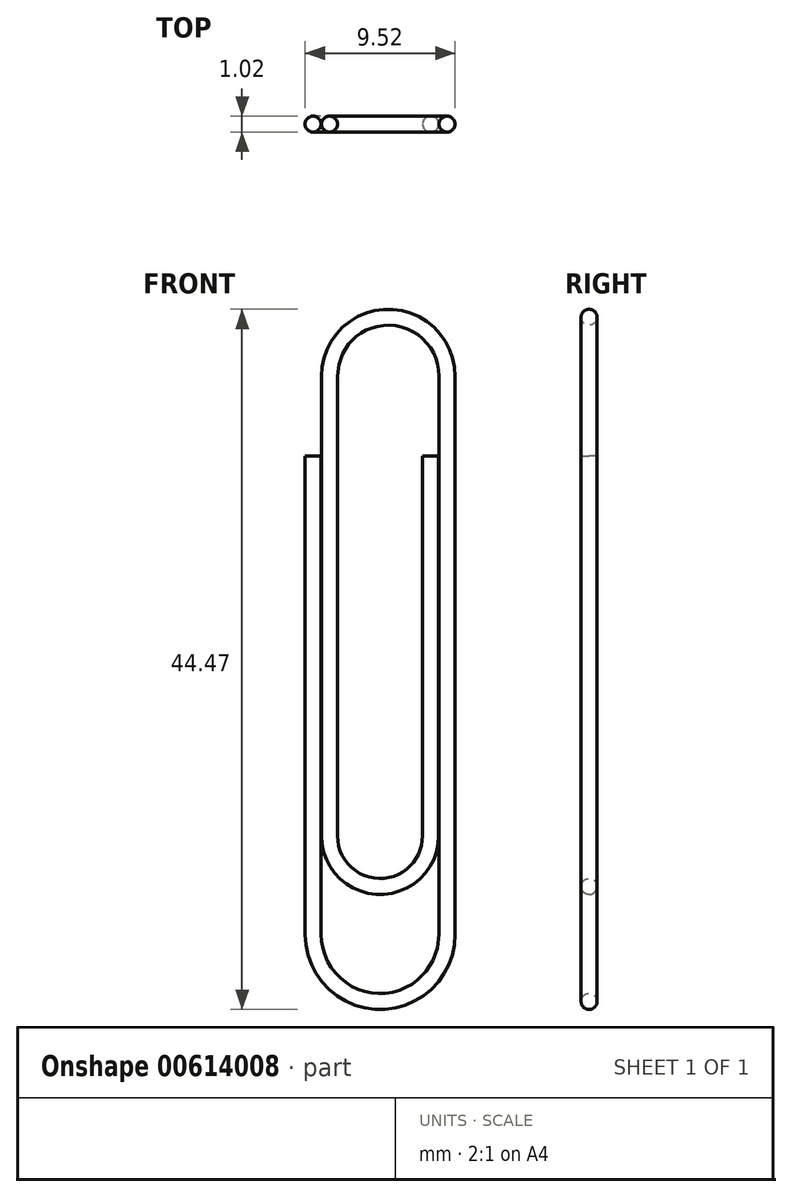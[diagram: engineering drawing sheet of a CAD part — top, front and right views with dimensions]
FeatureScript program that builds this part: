
annotation { "Feature Type Name" : "Feature", "Feature Type Description" : "" }
export const myFeature = defineFeature(function(context is Context, id is Id, definition is map)
    precondition{}
    {
        {
            var Q0;
            Q0=qCreatedBy(makeId("Front.planeOp"),FACE);
            var sketch = newSketch(context, id + "F0", { "sketchPlane" : qUnion([Q0])});
            skPoint(sketch, "E0", {"position": v(0, 0) * mm});
            skPoint(sketch, "E1", {"position": v(4.76, 0) * mm});
            skPoint(sketch, "E2", {"position": v(-4.76, 0) * mm});
            skLineSegment(sketch, "E3", {"start": v(-4.76, 0) * mm, "end": v(4.76, 0) * mm});
            skLineSegment(sketch, "E4", {"start": v(-4.76, 3.9) * mm, "end": v(-4.76, 34.3) * mm});
            skLineSegment(sketch, "E5", {"start": v(4.76, 3.9) * mm, "end": v(4.76, 39.37) * mm});
            skLineSegment(sketch, "E6.0", {"start": v(3.72, 10.16) * mm, "end": v(3.72, 34.3) * mm});
            skLineSegment(sketch, "E7.0", {"start": v(2.7, 10.16) * mm, "end": v(2.7, 34.3) * mm});
            skLineSegment(sketch, "E8.0", {"start": v(-3.72, 10.16) * mm, "end": v(-3.72, 39.37) * mm});
            skLineSegment(sketch, "E9.0", {"start": v(-2.7, 10.16) * mm, "end": v(-2.7, 39.37) * mm});
            skPoint(sketch, "E10", {"position": v(2.7, 34.3) * mm});
            skLineSegment(sketch, "E11", {"start": v(2.7, 34.3) * mm, "end": v(3.72, 34.3) * mm});
            skLineSegment(sketch, "E12", {"start": v(-3.75, 34.3) * mm, "end": v(-4.76, 34.3) * mm});
            skPoint(sketch, "E13", {"position": v(-2.7, 10.16) * mm});
            skPoint(sketch, "E14", {"position": v(2.7, 10.16) * mm});
            skPoint(sketch, "E15", {"position": v(0, 7.45) * mm});
            skArc(sketch, "E16", {"start": v(-2.7, 10.16) * mm, "mid": v(0, 7.45) * mm, "end": v(2.7, 10.16) * mm});
            skPoint(sketch, "E17", {"position": v(0, 6.44) * mm});
            skArc(sketch, "E18", {"start": v(-3.72, 10.16) * mm, "mid": v(0, 6.44) * mm, "end": v(3.72, 10.16) * mm});
            skPoint(sketch, "E19", {"position": v(0, 3.9) * mm});
            skArc(sketch, "E20", {"start": v(-4.76, 3.9) * mm, "mid": v(0, -0.86) * mm, "end": v(4.76, 3.9) * mm});
            skArc(sketch, "E21", {"start": v(-3.75, 3.9) * mm, "mid": v(0, 0.15) * mm, "end": v(3.75, 3.9) * mm});
            skLineSegment(sketch, "E22.trimOffspring", {"start": v(-3.75, 3.9) * mm, "end": v(-3.75, 34.3) * mm});
            skLineSegment(sketch, "E23.trimOffspring", {"start": v(3.75, 3.9) * mm, "end": v(3.75, 39.37) * mm});
            skArc(sketch, "E24", {"start": v(3.75, 39.37) * mm, "mid": v(0.52, 42.6) * mm, "end": v(-2.7, 39.37) * mm});
            skArc(sketch, "E25", {"start": v(4.76, 39.37) * mm, "mid": v(0.52, 43.61) * mm, "end": v(-3.72, 39.37) * mm});
            skSolve(sketch);
        }
        {
            var Q0;
            {var subQ4=sQuery(id+"F0.wireOp",EDGE,"E4");Q0=makeQuery(id+"F0.imprint","IMPRINT",FACE,{"disambiguationData":[TD([[makeQuery(id+"F0.imprint","IMPRINT",EDGE,{"derivedFrom":subQ4}),-1.0]])]});}
            extrude(context, id + "F1", {"entities" : qUnion([Q0]), "depth" : 1.02 * mm, "offsetDistance" : 25.4 * mm});
        }
        {
            var Q0;
            Q0 = qSketchRegion(id + "F0", true);
            extrude(context, id + "F2", {"entities" : qUnion([Q0]), "operationType" : NewBodyOperationType.ADD, "depth" : 1.02 * mm, "offsetDistance" : 25.4 * mm});
        }
        {
            var Q0;
            Q0=makeQuery(id+"F1.opExtrude","CAP_EDGE",EDGE,{"disambiguationData":[OSD([sQuery(id+"F0.wireOp",EDGE,"E5")])],"isStart":false});
            fillet(context, id + "F3", {"entities" : qUnion([Q0]), "radius" : 0.5 * mm, "tangentPropagation" : true, "allowEdgeOverflow" : false});
        }
        {
            var Q0;
            Q0=makeQuery(id+"F1.opExtrude","CAP_EDGE",EDGE,{"disambiguationData":[OSD([sQuery(id+"F0.wireOp",EDGE,"E5")])],"isStart":true});
            fillet(context, id + "F4", {"entities" : qUnion([Q0]), "radius" : 0.5 * mm, "tangentPropagation" : true, "allowEdgeOverflow" : false});
        }
        {
            var Q0;
            Q0=makeQuery(id+"F1.opExtrude","CAP_EDGE",EDGE,{"disambiguationData":[OSD([sQuery(id+"F0.wireOp",EDGE,"E23.trimOffspring")])],"isStart":true});
            fillet(context, id + "F5", {"entities" : qUnion([Q0]), "radius" : 0.5 * mm, "tangentPropagation" : true, "allowEdgeOverflow" : false});
        }
        {
            var Q0;
            Q0=makeQuery(id+"F1.opExtrude","CAP_EDGE",EDGE,{"disambiguationData":[OSD([sQuery(id+"F0.wireOp",EDGE,"E21")])],"isStart":false});
            var Q1;
            Q1=makeQuery(id+"F1.opExtrude","CAP_EDGE",EDGE,{"disambiguationData":[OSD([sQuery(id+"F0.wireOp",EDGE,"E23.trimOffspring")])],"isStart":false});
            fillet(context, id + "F6", {"entities" : qUnion([Q0, Q1]), "radius" : 0.5 * mm, "tangentPropagation" : true, "allowEdgeOverflow" : false});
        }
    });
